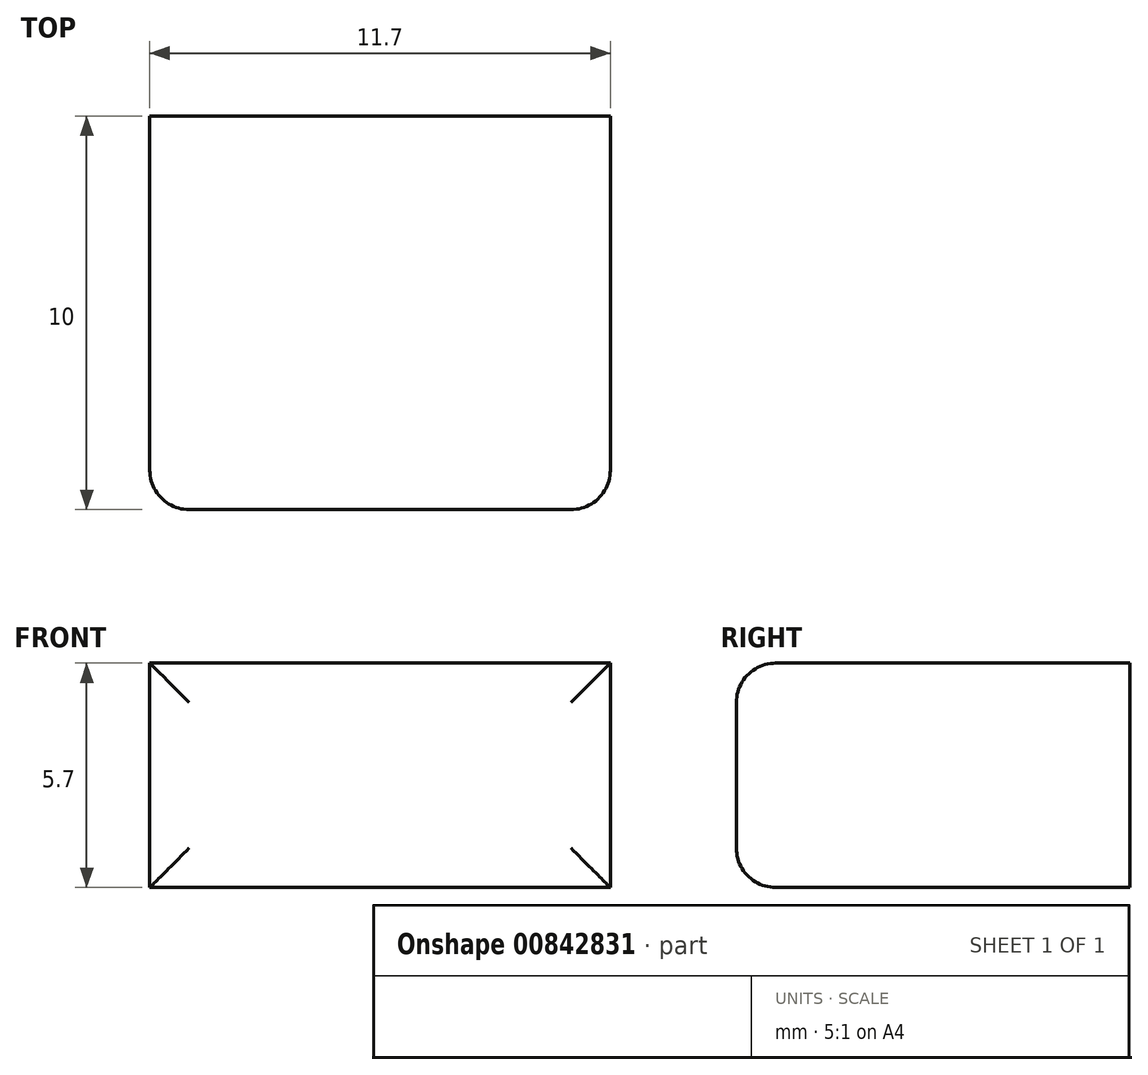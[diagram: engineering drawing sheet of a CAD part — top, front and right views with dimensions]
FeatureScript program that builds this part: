
annotation { "Feature Type Name" : "Feature", "Feature Type Description" : "" }
export const myFeature = defineFeature(function(context is Context, id is Id, definition is map)
    precondition{}
    {
        {
            var Q0;
            Q0=qCreatedBy(makeId("Front.planeOp"),FACE);
            var sketch = newSketch(context, id + "F0", { "sketchPlane" : qUnion([Q0])});
            skLineSegment(sketch, "E0.bottom", {"start": v(0, 0) * mm, "end": v(11.7, 0) * mm});
            skLineSegment(sketch, "E0.top", {"start": v(0, 5.7) * mm, "end": v(11.7, 5.7) * mm});
            skLineSegment(sketch, "E0.left", {"start": v(0, 0) * mm, "end": v(0, 5.7) * mm});
            skLineSegment(sketch, "E0.right", {"start": v(11.7, 0) * mm, "end": v(11.7, 5.7) * mm});
            skSolve(sketch);
        }
        {
            var Q0;
            Q0=makeQuery(id+"F0.imprint","IMPRINT",FACE,{"disambiguationData":[TD([[makeQuery(id+"F0.imprint","IMPRINT",EDGE,{"derivedFrom":sQuery(id+"F0.wireOp",EDGE,"E0.bottom")}),1.0]])]});
            extrude(context, id + "F1", {"entities" : qUnion([Q0]), "depth" : 10 * mm, "offsetDistance" : 25 * mm});
        }
        {
            var Q0;
            Q0=makeQuery(id+"F1.opExtrude","CAP_EDGE",EDGE,{"disambiguationData":[OSD([sQuery(id+"F0.wireOp",EDGE,"E0.top")])],"isStart":false});
            var Q1;
            Q1=makeQuery(id+"F1.opExtrude","CAP_EDGE",EDGE,{"disambiguationData":[OSD([sQuery(id+"F0.wireOp",EDGE,"E0.right")])],"isStart":false});
            var Q2;
            Q2=makeQuery(id+"F1.opExtrude","CAP_EDGE",EDGE,{"disambiguationData":[OSD([sQuery(id+"F0.wireOp",EDGE,"E0.bottom")])],"isStart":false});
            var Q3;
            Q3=makeQuery(id+"F1.opExtrude","CAP_EDGE",EDGE,{"disambiguationData":[OSD([sQuery(id+"F0.wireOp",EDGE,"E0.left")])],"isStart":false});
            fillet(context, id + "F2", {"entities" : qUnion([Q0, Q1, Q2, Q3]), "radius" : 1 * mm, "tangentPropagation" : true, "allowEdgeOverflow" : false});
        }
    });
